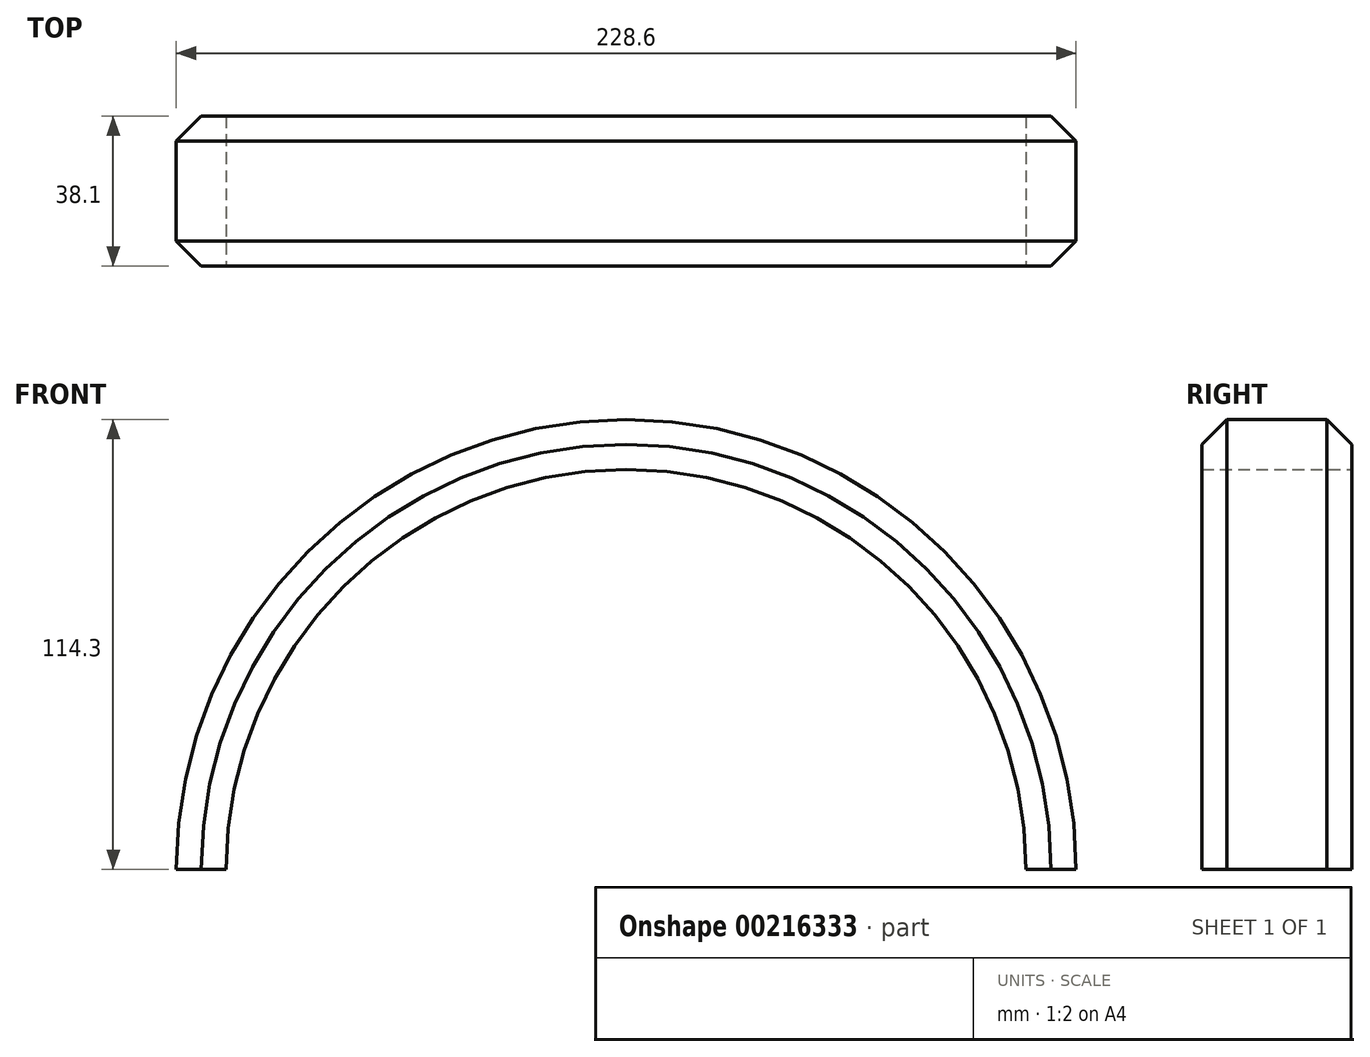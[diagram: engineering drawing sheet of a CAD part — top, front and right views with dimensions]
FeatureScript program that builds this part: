
annotation { "Feature Type Name" : "Feature", "Feature Type Description" : "" }
export const myFeature = defineFeature(function(context is Context, id is Id, definition is map)
    precondition{}
    {
        {
            var Q0;
            Q0=qCreatedBy(makeId("Top.planeOp"),FACE);
            var sketch = newSketch(context, id + "F0", { "sketchPlane" : qUnion([Q0])});
            skLineSegment(sketch, "E0", {"start": v(0, 120.33) * mm, "end": v(0, -110.2) * mm, "construction": true});
            skLineSegment(sketch, "E1", {"start": v(101.6, 19.05) * mm, "end": v(101.6, 0) * mm});
            skLineSegment(sketch, "E2", {"start": v(101.6, 0) * mm, "end": v(114.3, 0) * mm});
            skLineSegment(sketch, "E3", {"start": v(114.3, 0) * mm, "end": v(114.3, 12.7) * mm});
            skLineSegment(sketch, "E4", {"start": v(101.6, 19.05) * mm, "end": v(107.95, 19.05) * mm});
            skLineSegment(sketch, "E5", {"start": v(107.95, 19.05) * mm, "end": v(114.3, 12.7) * mm});
            skSolve(sketch);
        }
        {
            var Q0;
            Q0=makeQuery(id+"F0.imprint","IMPRINT",FACE,{"disambiguationData":[TD([[makeQuery(id+"F0.imprint","IMPRINT",EDGE,{"derivedFrom":sQuery(id+"F0.wireOp",EDGE,"E1")}),1.0]])]});
            var Q1;
            Q1=qBodyType(qCreatedBy(id+"F0",EDGE),BodyType.WIRE);
            var Q2;
            Q2=sQuery(id+"F0.wireOp",EDGE,"E0");
            revolve(context, id + "F1", {"entities" : qUnion([Q0]), "surfaceEntities" : qUnion([Q1]), "axis" : qUnion([Q2]), "revolveType" : RevolveType.ONE_DIRECTION, "angle" : 180 * degree});
        }
        {
            var Q0;
            Q0=makeQuery(id+"F1.opRevolve","SWEPT_BODY",BODY,{"disambiguationData":[OSD([sQuery(id+"F0.wireOp",EDGE,"E1"),sQuery(id+"F0.wireOp",EDGE,"E2"),sQuery(id+"F0.wireOp",EDGE,"E3"),sQuery(id+"F0.wireOp",EDGE,"E4"),sQuery(id+"F0.wireOp",EDGE,"E5")])]});
            var Q1;
            Q1=qCreatedBy(makeId("Front.planeOp"),FACE);
            mirror(context, id + "F2", {"operationType" : NewBodyOperationType.ADD, "entities" : qUnion([Q0]), "mirrorPlane" : qUnion([Q1])});
        }
    });
